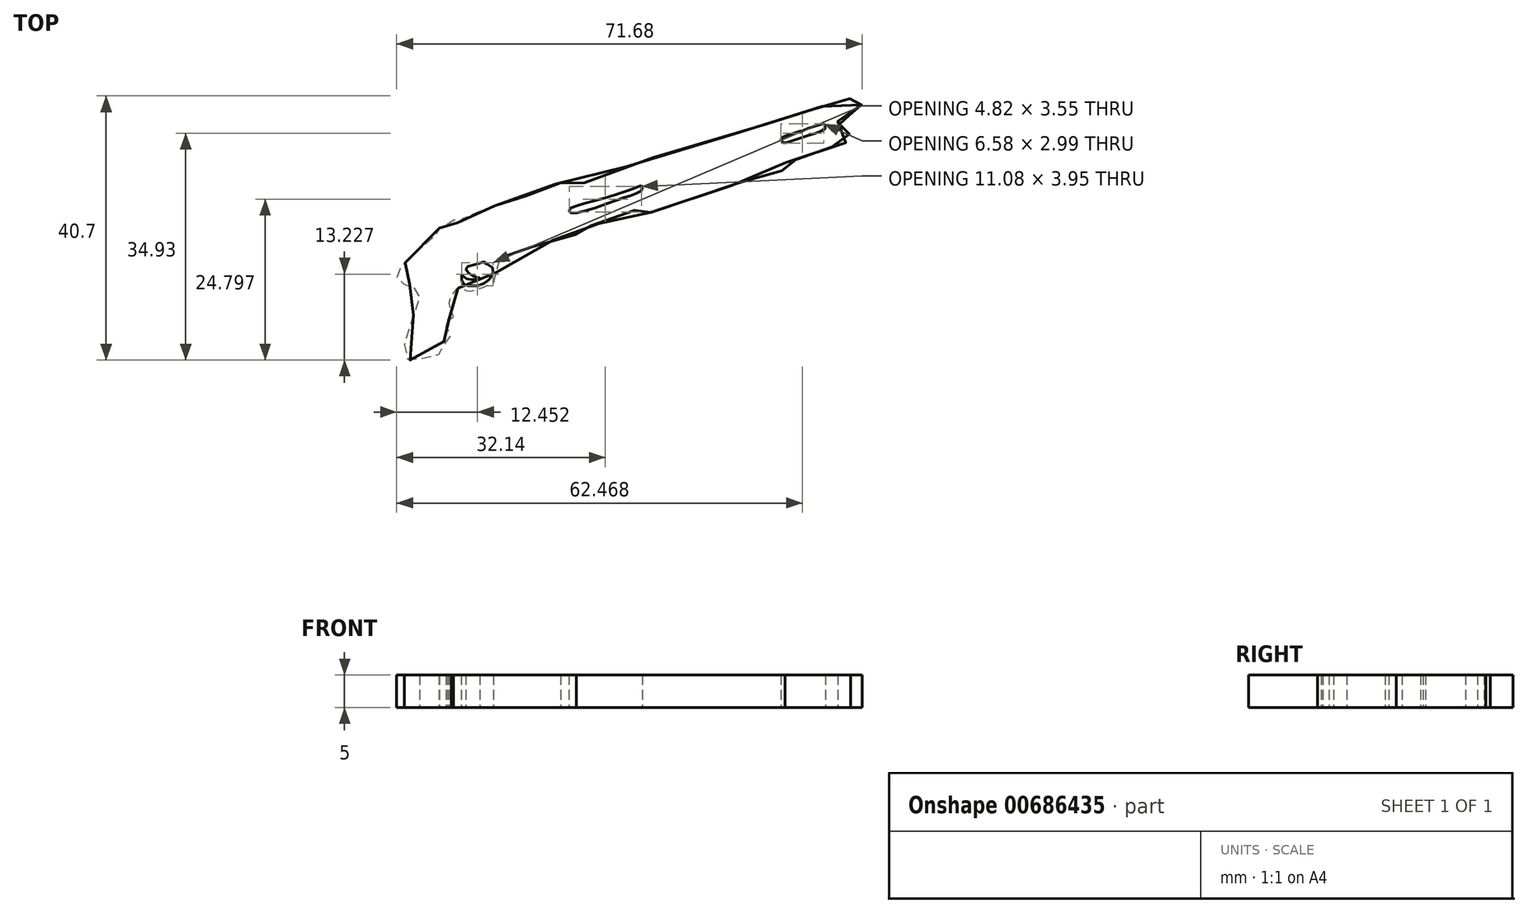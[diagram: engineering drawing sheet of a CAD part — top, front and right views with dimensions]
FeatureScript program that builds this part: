
annotation { "Feature Type Name" : "Feature", "Feature Type Description" : "" }
export const myFeature = defineFeature(function(context is Context, id is Id, definition is map)
    precondition{}
    {
        {
            var Q0;
            Q0=qCreatedBy(makeId("Top.planeOp"),FACE);
            var sketch = newSketch(context, id + "F0", { "sketchPlane" : qUnion([Q0])});
            skFitSpline(sketch, "E0", {"points": [v(-57.45, 25.41) * mm, v(-59.59, 24.58) * mm, v(-62.08, 23.51) * mm, v(-63.04, 23.13) * mm, v(-63.12, 22.8) * mm, v(-63.27, 22.67) * mm, v(-63.4, 22.69) * mm, v(-63.48, 22.95) * mm, v(-63.57, 23.24) * mm, v(-63.8, 23.15) * mm, v(-64.05, 23) * mm, v(-64.52, 22.72) * mm, v(-66, 21.92) * mm, v(-66, 21.86) * mm, v(-65.94, 21.33) * mm, v(-66.69, 20.76) * mm, v(-70.73, 17.1) * mm, v(-72.35, 15.34) * mm, v(-72.5, 14.51) * mm, v(-72.09, 13.8) * mm, v(-71.35, 13.36) * mm, v(-70.28, 13.2) * mm, v(-69.25, 11.84) * mm, v(-68.96, 11.37) * mm, v(-69.25, 10.16) * mm, v(-69.56, 9.65) * mm, v(-71.1, 4.95) * mm, v(-71.35, 4) * mm, v(-70.9, 1.9) * mm, v(-70.48, 1.65) * mm, v(-67.36, 2.18) * mm, v(-65.72, 2.55) * mm, v(-65.43, 2.68) * mm, v(-64.98, 5.1) * mm, v(-64.12, 5.51) * mm, v(-64.82, 6.3) * mm, v(-64.82, 6.95) * mm, v(-64.65, 7.44) * mm, v(-64.61, 7.81) * mm, v(-63.83, 8.26) * mm, v(-64.04, 8.96) * mm, v(-64.2, 9.54) * mm, v(-64.32, 10.9) * mm, v(-62.68, 12.86) * mm, v(-61.61, 12.29) * mm, v(-57.59, 13.64) * mm, v(-57.46, 13.89) * mm, v(-56.44, 17.55) * mm, v(-55.78, 17.75) * mm, v(-47.97, 20.26) * mm, v(-44.85, 21.16) * mm, v(-44.85, 21.65) * mm, v(-43.46, 22.15) * mm, v(-36.88, 24.28) * mm, v(-34.1, 25.18) * mm, v(-33.72, 24.45) * mm, v(-32.61, 24.7) * mm, v(-24.32, 27.36) * mm, v(-16.88, 29.83) * mm, v(-12.79, 31.15) * mm, v(-12.72, 31.98) * mm, v(-10.78, 32.57) * mm, v(-6.16, 34.3) * mm, v(-2.7, 35.52) * mm, v(-2.8, 36.34) * mm, v(-3.53, 38.09) * mm, v(-3.96, 38.11) * mm, v(-4.33, 37.93) * mm, v(-4.6, 38.8) * mm, v(-4.1, 38.9) * mm, v(-2.38, 39.57) * mm, v(-0.93, 40.02) * mm, v(-0.93, 40.85) * mm, v(-1.14, 41.28) * mm, v(-1.92, 42.34) * mm, v(-2.6, 42) * mm, v(-6.54, 40.82) * mm, v(-13.6, 38.6) * mm, v(-23.81, 35.57) * mm, v(-36.8, 31.56) * mm, v(-47.23, 28.24) * mm, v(-47.3, 28.87) * mm, v(-49.3, 28.17) * mm, v(-54.76, 26.24) * mm, v(-57.45, 25.41) * mm]});
            skFitSpline(sketch, "E1", {"points": [v(-35.24, 28.42) * mm, v(-41.73, 26.24) * mm, v(-45.91, 24.83) * mm, v(-45.74, 24.35) * mm, v(-40.2, 25.72) * mm, v(-37, 26.82) * mm, v(-34.72, 27.94) * mm, v(-34.86, 28.5) * mm, v(-35.24, 28.42) * mm]});
            skFitSpline(sketch, "E2", {"points": [v(-10.1, 36.9) * mm, v(-10.55, 36.9) * mm, v(-11.43, 36.53) * mm, v(-13.34, 35.8) * mm, v(-13.16, 35.3) * mm, v(-13.01, 35.1) * mm, v(-10.77, 35.71) * mm, v(-6.6, 37.25) * mm, v(-6.57, 37.56) * mm, v(-6.76, 38.07) * mm, v(-7.3, 37.95) * mm, v(-9.5, 37.22) * mm, v(-10.1, 36.9) * mm]});
            skFitSpline(sketch, "E3", {"points": [v(-62.48, 14.75) * mm, v(-62.53, 13.87) * mm, v(-62.32, 13.5) * mm, v(-61.88, 13.16) * mm, v(-61.36, 13.1) * mm, v(-60.72, 13.08) * mm, v(-60.01, 13.11) * mm, v(-59.11, 13.44) * mm, v(-58.5, 13.87) * mm, v(-57.92, 14.5) * mm, v(-57.66, 14.85) * mm, v(-57.7, 15.4) * mm, v(-57.83, 15.96) * mm, v(-58.63, 16.5) * mm, v(-59.18, 16.79) * mm, v(-59.89, 16.53) * mm, v(-60.3, 16.46) * mm, v(-61.27, 16.1) * mm, v(-61.79, 16) * mm, v(-61.79, 15.44) * mm, v(-61.4, 15.06) * mm, v(-60.96, 14.68) * mm, v(-59.75, 14.3) * mm, v(-59.73, 14.16) * mm, v(-60.17, 14.03) * mm, v(-61.12, 14.04) * mm, v(-61.77, 14.16) * mm, v(-62.48, 14.75) * mm]});
            skSolve(sketch);
        }
        {
            var Q0;
            Q0 = qSketchRegion(id + "F0", true);
            extrude(context, id + "F1", {"entities" : qUnion([Q0]), "depth" : 5 * mm, "offsetDistance" : 25.4 * mm});
        }
    });
